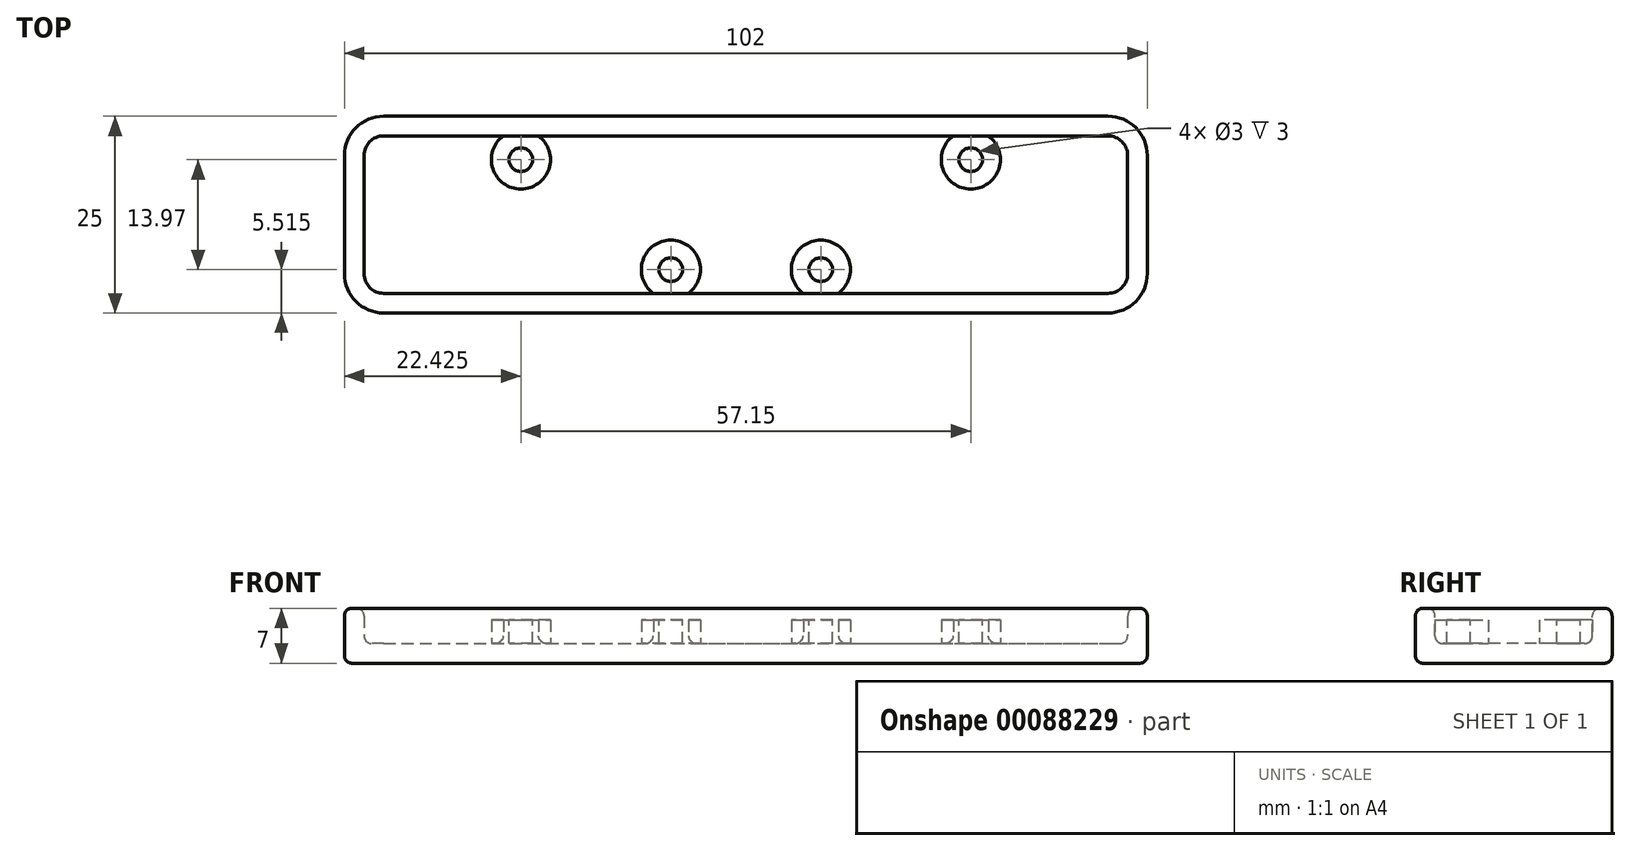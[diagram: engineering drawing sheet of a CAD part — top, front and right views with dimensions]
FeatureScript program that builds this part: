
annotation { "Feature Type Name" : "Feature", "Feature Type Description" : "" }
export const myFeature = defineFeature(function(context is Context, id is Id, definition is map)
    precondition{}
    {
        {
            var Q0;
            Q0=qCreatedBy(makeId("Top.planeOp"),FACE);
            var sketch = newSketch(context, id + "F0", { "sketchPlane" : qUnion([Q0])});
            skLineSegment(sketch, "E0.bottom", {"start": v(-51, 12.5) * mm, "end": v(51, 12.5) * mm});
            skLineSegment(sketch, "E0.top", {"start": v(-51, -12.5) * mm, "end": v(51, -12.5) * mm});
            skLineSegment(sketch, "E0.left", {"start": v(-51, 12.5) * mm, "end": v(-51, -12.5) * mm});
            skLineSegment(sketch, "E0.right", {"start": v(51, 12.5) * mm, "end": v(51, -12.5) * mm});
            skPoint(sketch, "E1", {"position": v(0, 12.5) * mm});
            skPoint(sketch, "E2", {"position": v(51, 0) * mm});
            skSolve(sketch);
        }
        {
            var Q0;
            Q0=qSketchRegion(id+"F0",true);
            extrude(context, id + "F1", {"entities" : qUnion([Q0]), "depth" : 7 * mm});
        }
        {
            var Q0;
            Q0=makeQuery(id+"F1.opExtrude","SWEPT_EDGE",EDGE,{"disambiguationData":[OSD([sQuery(id+"F0.wireOp",EDGE,"E0.top"),sQuery(id+"F0.wireOp",EDGE,"E0.left")])]});
            var Q1;
            Q1=makeQuery(id+"F1.opExtrude","SWEPT_EDGE",EDGE,{"disambiguationData":[OSD([sQuery(id+"F0.wireOp",EDGE,"E0.bottom"),sQuery(id+"F0.wireOp",EDGE,"E0.left")])]});
            var Q2;
            Q2=makeQuery(id+"F1.opExtrude","SWEPT_EDGE",EDGE,{"disambiguationData":[OSD([sQuery(id+"F0.wireOp",EDGE,"E0.top"),sQuery(id+"F0.wireOp",EDGE,"E0.right")])]});
            var Q3;
            Q3=makeQuery(id+"F1.opExtrude","SWEPT_EDGE",EDGE,{"disambiguationData":[OSD([sQuery(id+"F0.wireOp",EDGE,"E0.bottom"),sQuery(id+"F0.wireOp",EDGE,"E0.right")])]});
            fillet(context, id + "F2", {"entities" : qUnion([Q0, Q1, Q2, Q3]), "radius" : 5 * mm, "tangentPropagation" : true, "allowEdgeOverflow" : false});
        }
        {
            var Q0;
            Q0=makeQuery(id+"F1.opExtrude","CAP_FACE",FACE,{"disambiguationData":[OSD([sQuery(id+"F0.wireOp",EDGE,"E0.bottom"),sQuery(id+"F0.wireOp",EDGE,"E0.top"),sQuery(id+"F0.wireOp",EDGE,"E0.left"),sQuery(id+"F0.wireOp",EDGE,"E0.right")])],"isStart":false});
            shell(context, id + "F3", {"entities" : qUnion([Q0]), "thickness" : 2.5 * mm});
        }
        {
            var Q0;
            Q0=makeQuery(id+"F3.opShell","OFFSET_FACE",FACE,{"disambiguationData":[OSD([sQuery(id+"F0.wireOp",EDGE,"E0.bottom"),sQuery(id+"F0.wireOp",EDGE,"E0.top"),sQuery(id+"F0.wireOp",EDGE,"E0.left"),sQuery(id+"F0.wireOp",EDGE,"E0.right")])]});
            var Q1;
            Q1=makeQuery(id+"F1.opExtrude","CAP_FACE",FACE,{"disambiguationData":[OSD([sQuery(id+"F0.wireOp",EDGE,"E0.bottom"),sQuery(id+"F0.wireOp",EDGE,"E0.top"),sQuery(id+"F0.wireOp",EDGE,"E0.left"),sQuery(id+"F0.wireOp",EDGE,"E0.right")])],"isStart":false});
            var Q2;
            Q2=makeQuery(id+"F1.opExtrude","CAP_FACE",FACE,{"disambiguationData":[OSD([sQuery(id+"F0.wireOp",EDGE,"E0.bottom"),sQuery(id+"F0.wireOp",EDGE,"E0.top"),sQuery(id+"F0.wireOp",EDGE,"E0.left"),sQuery(id+"F0.wireOp",EDGE,"E0.right")])],"isStart":true});
            fillet(context, id + "F4", {"entities" : qUnion([Q0, Q1, Q2]), "radius" : 1 * mm, "tangentPropagation" : true, "allowEdgeOverflow" : false});
        }
        {
            var Q0;
            Q0=makeQuery(id+"F3.opShell","OFFSET_FACE",FACE,{"disambiguationData":[OSD([sQuery(id+"F0.wireOp",EDGE,"E0.bottom"),sQuery(id+"F0.wireOp",EDGE,"E0.top"),sQuery(id+"F0.wireOp",EDGE,"E0.left"),sQuery(id+"F0.wireOp",EDGE,"E0.right")])]});
            var sketch = newSketch(context, id + "F5", { "sketchPlane" : qUnion([Q0])});
            skCircle(sketch, "E3", {"center": v(-9.52, -6.99) * mm, "radius": 3.75 * mm});
            skLineSegment(sketch, "E4", {"start": v(0, 4.17) * mm, "end": v(0, -3.94) * mm, "construction": true});
            skCircle(sketch, "E5.MirrorC", {"center": v(9.52, -6.99) * mm, "radius": 3.75 * mm});
            skCircle(sketch, "E6", {"center": v(-28.57, 6.98) * mm, "radius": 3.75 * mm});
            skCircle(sketch, "E7.MirrorC", {"center": v(28.57, 6.98) * mm, "radius": 3.75 * mm});
            skSolve(sketch);
        }
        {
            var Q0;
            Q0=qSketchRegion(id+"F5",true);
            extrude(context, id + "F6", {"entities" : qUnion([Q0]), "operationType" : NewBodyOperationType.ADD, "depth" : 3 * mm});
        }
        {
            var Q0;
            Q0=makeQuery(id+"F6.opExtrude","CAP_FACE",FACE,{"disambiguationData":[OSD([sQuery(id+"F5.wireOp",EDGE,"E3")])],"isStart":false});
            var sketch = newSketch(context, id + "F7", { "sketchPlane" : qUnion([Q0])});
            skCircle(sketch, "E8", {"center": v(-9.52, -6.99) * mm, "radius": 1.5 * mm});
            skCircle(sketch, "E9", {"center": v(-28.57, 6.98) * mm, "radius": 1.5 * mm});
            skCircle(sketch, "E10.MirrorC", {"center": v(9.52, -6.99) * mm, "radius": 1.5 * mm});
            skCircle(sketch, "E11.MirrorC", {"center": v(28.57, 6.98) * mm, "radius": 1.5 * mm});
            skSolve(sketch);
        }
        {
            var Q0;
            Q0=qSketchRegion(id+"F7",true);
            var Q1;
            Q1=makeQuery(id+"F3.opShell","OFFSET_FACE",FACE,{"disambiguationData":[OSD([sQuery(id+"F0.wireOp",EDGE,"E0.bottom"),sQuery(id+"F0.wireOp",EDGE,"E0.top"),sQuery(id+"F0.wireOp",EDGE,"E0.left"),sQuery(id+"F0.wireOp",EDGE,"E0.right")])]});
            extrude(context, id + "F8", {"entities" : qUnion([Q0]), "operationType" : NewBodyOperationType.REMOVE, "endBound" : BoundingType.UP_TO_SURFACE, "oppositeDirection" : true, "endBoundEntityFace" : qUnion([Q1]), "depth" : 25 * mm});
        }
    });
